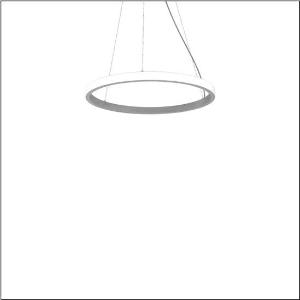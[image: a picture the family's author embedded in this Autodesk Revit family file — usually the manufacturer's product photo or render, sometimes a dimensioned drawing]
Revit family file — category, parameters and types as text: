
# Revit family: silica_r__21_ring-o_5pjbo2d1204a_bf82
name_source: partatom
category: Lighting Fixtures
units: mm (PartAtom-declared; Revit-internal decimal feet)

## family parameters
Cut with Voids When Loaded = No
Host = Face
Light Source = No
Part Type = Normal
Room Calculation Point = No
Round Connector Dimension = Use Diameter
Shared = No

## types (1)
- Silica® 21 Ring-O (1 x LED, 4700 lm, 80 W, 3000K)
    Apparent Load = 80 VA
    CIE Flux Codes = 2 16 49 50 100
    Color Rendering = 80
    Color Temperature = 3000K
    Default Elevation = 1800 mm
    Description = Silica® 21 Ring-O, suspended luminaire, of PMMA, frosted, light emission: outer ring side luminous distribution, primary light characteristic: symmetric, installation type: suspended mounting, LED, rated luminous flux: 4.700lm, luminous efficacy: 59lm/W, light colour: 830, colour temperature: 3000K, with terminal, 5-pole, mains connection: 230V, AC/DC, 0/50..60Hz, rated input power: 80W, housing, of extruded aluminium section, metallic grey (RAL 9006), diameter: 810mm, ceiling canopy, metallic grey (RAL 9006), protection rating (lamp compartment): IP40, insulation class (complete): insulation class I (protective earthing), certification: CE, impact resistance: IK02, permissible operating ambient temperature: 0..+35°C, packaging unit: 1 piece
    Height = 48 mm  [stored 0.15748 ft]
    Lamp = 1 x LED
    Lamp Light Flux = 4700 lm
    Lamp Power = 80 W
    Lamp count = 1
    Length = 810 mm
    Luminous efficacy = 59 lm/W
    Manufacturer = Siteco
    ModVariant = No
    Model = 5PJBO2D1204A
    Mounting Place = Ceiling
    Mounting Type = Pendant
    Number of Poles = 1
    OnlyDefault = Yes
    Power Factor = 1
    Product Name = Silica® 21 Ring-O
    Product group = suspended luminaire
    ProductGroupID = 904
    Protection Class = Protection class I
    Protection Degree = IP 40
    RLX_Detail_Level = 1
    RLX_Emergency_Light_Flux = 0 lm
    RLX_Emergency_Type = 0
    RLX_Emergency_Type_DB = No
    RlxData = <blob elided: 13041 chars, md5=9430033b>
    Socket = socket
    Standby Power = 0 W
    System Light Flux = 4700 lm
    System Power = 80 W
    Type Comments = Product without accessories
    Type Image = l_1251760.jpg
    URL = http://relux.com
    VarID = ---
    Voltage = 0 V
    Weight = 0.00 kg
    Width = 0 mm  [stored 0 ft]

note: [stored X ft] marks values corroborated as IEEE doubles in the binary element streams (Revit-internal decimal feet)

## geometry (parser evidence)
native form markers: Sweep x10
no freeform markers — native parametric forms only
